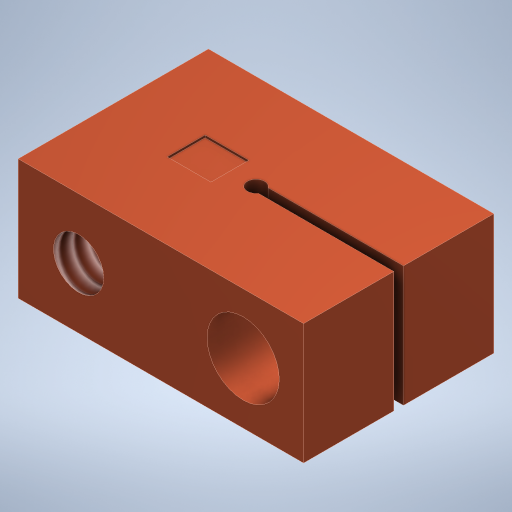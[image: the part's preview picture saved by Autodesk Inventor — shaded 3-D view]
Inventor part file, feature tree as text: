
AUTODESK INVENTOR PART (.ipt)
format: ipt  version: 2024 (Build 280153000, 153)  size: 302,080 bytes
history: native  units: in
note: dims shown in document units (in); Inventor stores cm internally (conversion verified against a paired STEP export)
features: sketch x6, extrude x3, hole x3, other x2
ambient origin geometry x8: Origin, YZ Plane, XZ Plane, XY Plane, X Axis, Y Axis, Z Axis, Center Point
bodies: Solid1 (feature_tree)
feature tree (14):
  other  "Annotations"
  extrude  "Extrusion1"  Depth=0.3937in
  sketch  "Sketch2"  dims[d2=0.2953in d3=0.036in]
  extrude  "Extrusion2"  Depth=0.036in
  hole  "Hole3"  [1 undecoded]
  hole  "Hole4"  [1 undecoded]
  hole  "Hole5"  [1 undecoded]
  sketch  "Sketch5"  dims[d9=0.138in d10=45.0deg]
  extrude  "Extrusion4"  Depth=0.3937in
  sketch  "Sketch1"  dims[d0=0.5906in d1=0.3937in]
  sketch  "Sketch3"  dims[d4=0.01in d5=0.01in]
  sketch  "Sketch4"  dims[d6=0.25in d7=0.0in d8=135.0deg]
  sketch  "Sketch6"  dims[d11=0.138in d30=0.04in d31=0.1378in d32=0.0in d35=0.104in d36=0.276in d37=0.375in d38=0.25in d39=0.5635in d40=1.0in d41=0.8108in d44=45.0deg d45=0.104in d46=0.104in d47=0.1969in d48=0.375in d49=0.25in d50=0.5635in d51=0.1969in d52=0.8108in d53=0.1495in d54=0.276in d55=0.279in d56=0.25in d57=0.5635in d58=0.1969in d59=0.8108in d60=0.3in d61=1.3in d62=0.25in d63=0.25in d64=0.25in d65=0.25in d66=1.451in d68=0.113in d69=0.113in d70=0.036in d79=0.0392in d80=0.0906in d81=0.0784in d82=0.005in d83=0.0in d84=0.3937in d42=1.8447in d43=0.104in]
  other  "Diameter Dimension 1"
note: 3 required parameter values undecoded (feature->parameter linkage not recoverable at this tier; creation-order binding heuristic only, values carry confidence <= 0.55)
